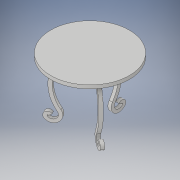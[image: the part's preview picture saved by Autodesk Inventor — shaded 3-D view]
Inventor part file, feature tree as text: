
AUTODESK INVENTOR PART (.ipt)
format: ipt  version: 2017 (Build 210142000, 142)  size: 201,216 bytes
history: native  units: in
note: dims shown in document units (in); Inventor stores cm internally (conversion verified against a paired STEP export)
features: sketch x2, extrude x1, pattern_circular x1, revolve x1
ambient origin geometry x8: Origin, YZ Plane, XZ Plane, XY Plane, X Axis, Y Axis, Z Axis, Center Point
bodies: Solid1 (feature_tree)
feature tree (5):
  extrude  "leg"  Depth=0.026in
  pattern_circular  "Circular Pattern1"  Count=3 Angle=360.0deg
  revolve  "Revolution1"  [1 undecoded]
  sketch  "Sketch1"  dims[d10=0.026in d11=0.026in d12=0.026in d15=0.026in]
  sketch  "Sketch2"  dims[d16=0.026in d17=0.0in d18=1.1811in d19=360.0deg d21=0.028in d22=0.119in d23=0.2in d24=90.0deg]
note: 1 required parameter value undecoded (feature->parameter linkage not recoverable at this tier; creation-order binding heuristic only, values carry confidence <= 0.55)
